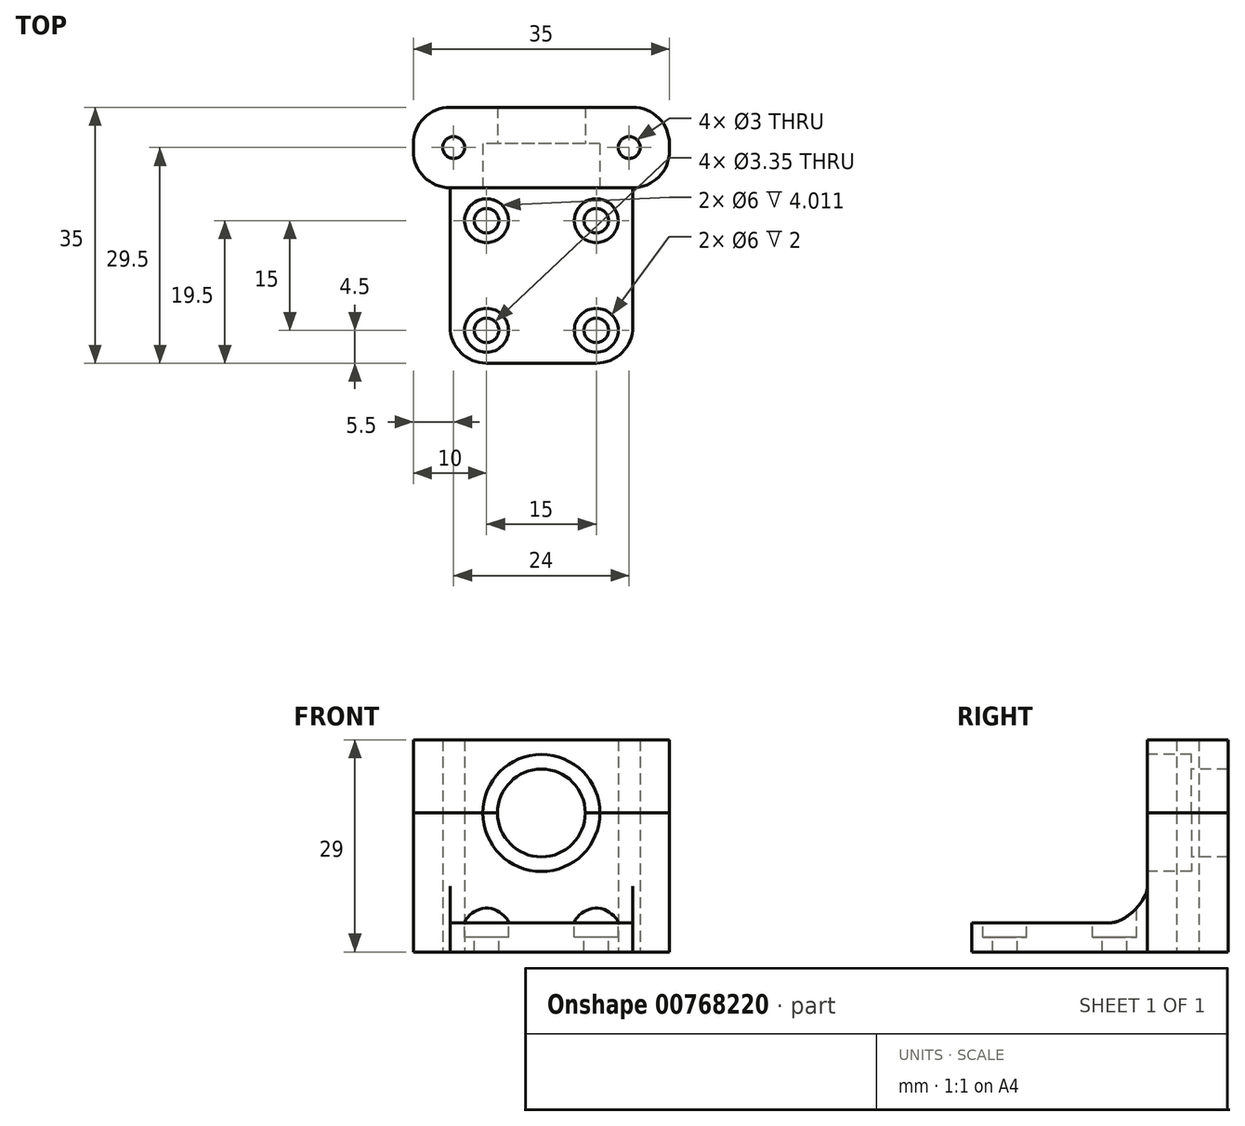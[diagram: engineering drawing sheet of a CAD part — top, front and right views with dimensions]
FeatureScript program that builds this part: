
annotation { "Feature Type Name" : "Feature", "Feature Type Description" : "" }
export const myFeature = defineFeature(function(context is Context, id is Id, definition is map)
    precondition{}
    {
        {
            var Q0;
            Q0=qCreatedBy(makeId("Right.planeOp"),FACE);
            var sketch = newSketch(context, id + "F0", { "sketchPlane" : qUnion([Q0])});
            skLineSegment(sketch, "E0", {"start": v(-12, -2) * mm, "end": v(23, -2) * mm});
            skLineSegment(sketch, "E1", {"start": v(23, -2) * mm, "end": v(23, 17) * mm});
            skLineSegment(sketch, "E2", {"start": v(23, 17) * mm, "end": v(12, 17) * mm});
            skLineSegment(sketch, "E3", {"start": v(12, 17) * mm, "end": v(12, 2) * mm});
            skLineSegment(sketch, "E4", {"start": v(12, 2) * mm, "end": v(-12, 2) * mm});
            skLineSegment(sketch, "E5", {"start": v(-12, 2) * mm, "end": v(-12, -2) * mm});
            skSolve(sketch);
        }
        {
            var Q0;
            Q0 = qSketchRegion(id + "F0", true);
            extrude(context, id + "F1", {"entities" : qUnion([Q0]), "endBound" : BoundingType.SYMMETRIC, "depth" : 25 * mm, "offsetDistance" : 25 * mm});
        }
        {
            var Q0;
            Q0=makeQuery(id+"F1.opExtrude","SWEPT_FACE",FACE,{"disambiguationData":[OSD([sQuery(id+"F0.wireOp",EDGE,"E0")])]});
            var sketch = newSketch(context, id + "F2", { "sketchPlane" : qUnion([Q0])});
            skLineSegment(sketch, "E6.bottom", {"start": v(-17.5, -23) * mm, "end": v(17.5, -23) * mm});
            skLineSegment(sketch, "E6.top", {"start": v(-17.5, -12) * mm, "end": v(17.5, -12) * mm});
            skLineSegment(sketch, "E6.left", {"start": v(-17.5, -23) * mm, "end": v(-17.5, -12) * mm});
            skLineSegment(sketch, "E6.right", {"start": v(17.5, -23) * mm, "end": v(17.5, -12) * mm});
            skSolve(sketch);
        }
        {
            var Q0;
            Q0 = qSketchRegion(id + "F2", true);
            var Q1;
            Q1=makeQuery(id+"F1.opExtrude","SWEPT_FACE",FACE,{"disambiguationData":[OSD([sQuery(id+"F0.wireOp",EDGE,"E2")])]});
            extrude(context, id + "F3", {"entities" : qUnion([Q0]), "operationType" : NewBodyOperationType.ADD, "endBound" : BoundingType.UP_TO_SURFACE, "oppositeDirection" : true, "depth" : 25 * mm, "endBoundEntityFace" : qUnion([Q1]), "offsetDistance" : 25 * mm});
        }
        {
            var Q0;
            Q0=makeQuery(id+"F1.opExtrude","SWEPT_FACE",FACE,{"disambiguationData":[OSD([sQuery(id+"F0.wireOp",EDGE,"E4")])]});
            var sketch = newSketch(context, id + "F4", { "sketchPlane" : qUnion([Q0])});
            skLineSegment(sketch, "E7.bottom", {"start": v(7.5, -7.5) * mm, "end": v(-7.5, -7.5) * mm, "construction": true});
            skLineSegment(sketch, "E7.top", {"start": v(7.5, 7.5) * mm, "end": v(-7.5, 7.5) * mm, "construction": true});
            skLineSegment(sketch, "E7.left", {"start": v(7.5, -7.5) * mm, "end": v(7.5, 7.5) * mm, "construction": true});
            skLineSegment(sketch, "E7.right", {"start": v(-7.5, -7.5) * mm, "end": v(-7.5, 7.5) * mm, "construction": true});
            skPoint(sketch, "E7.middle", {"position": v(0, 0) * mm});
            skCircle(sketch, "E8", {"center": v(7.5, 7.5) * mm, "radius": 3 * mm});
            skCircle(sketch, "E9", {"center": v(7.5, 7.5) * mm, "radius": 1.68 * mm});
            skCircle(sketch, "E10", {"center": v(7.5, -7.5) * mm, "radius": 3 * mm});
            skCircle(sketch, "E11", {"center": v(7.5, -7.5) * mm, "radius": 1.68 * mm});
            skCircle(sketch, "E12", {"center": v(-7.5, -7.5) * mm, "radius": 3 * mm});
            skCircle(sketch, "E13", {"center": v(-7.5, -7.5) * mm, "radius": 1.68 * mm});
            skCircle(sketch, "E14", {"center": v(-7.5, 7.5) * mm, "radius": 3 * mm});
            skCircle(sketch, "E15", {"center": v(-7.5, 7.5) * mm, "radius": 1.68 * mm});
            skSolve(sketch);
        }
        {
            var Q0;
            Q0=makeQuery(id+"F4.imprint","IMPRINT",FACE,{"disambiguationData":[TD([[makeQuery(id+"F4.imprint","IMPRINT",EDGE,{"derivedFrom":sQuery(id+"F4.wireOp",EDGE,"E9")}),1.0]])]});
            var Q1;
            Q1=makeQuery(id+"F4.imprint","IMPRINT",FACE,{"disambiguationData":[TD([[makeQuery(id+"F4.imprint","IMPRINT",EDGE,{"derivedFrom":sQuery(id+"F4.wireOp",EDGE,"E11")}),1.0]])]});
            var Q2;
            Q2=makeQuery(id+"F4.imprint","IMPRINT",FACE,{"disambiguationData":[TD([[makeQuery(id+"F4.imprint","IMPRINT",EDGE,{"derivedFrom":sQuery(id+"F4.wireOp",EDGE,"E13")}),1.0]])]});
            var Q3;
            Q3=makeQuery(id+"F4.imprint","IMPRINT",FACE,{"disambiguationData":[TD([[makeQuery(id+"F4.imprint","IMPRINT",EDGE,{"derivedFrom":sQuery(id+"F4.wireOp",EDGE,"E15")}),1.0]])]});
            extrude(context, id + "F5", {"entities" : qUnion([Q0, Q1, Q2, Q3]), "operationType" : NewBodyOperationType.REMOVE, "endBound" : BoundingType.THROUGH_ALL, "oppositeDirection" : true, "depth" : 25 * mm, "offsetDistance" : 25 * mm});
        }
        {
            var Q0;
            Q0=makeQuery(id+"F4.imprint","IMPRINT",FACE,{"disambiguationData":[TD([[makeQuery(id+"F4.imprint","IMPRINT",EDGE,{"derivedFrom":sQuery(id+"F4.wireOp",EDGE,"E14")}),1.0]])]});
            var Q1;
            Q1=makeQuery(id+"F4.imprint","IMPRINT",FACE,{"disambiguationData":[TD([[makeQuery(id+"F4.imprint","IMPRINT",EDGE,{"derivedFrom":sQuery(id+"F4.wireOp",EDGE,"E8")}),1.0]])]});
            var Q2;
            Q2=makeQuery(id+"F4.imprint","IMPRINT",FACE,{"disambiguationData":[TD([[makeQuery(id+"F4.imprint","IMPRINT",EDGE,{"derivedFrom":sQuery(id+"F4.wireOp",EDGE,"E10")}),1.0]])]});
            var Q3;
            Q3=makeQuery(id+"F4.imprint","IMPRINT",FACE,{"disambiguationData":[TD([[makeQuery(id+"F4.imprint","IMPRINT",EDGE,{"derivedFrom":sQuery(id+"F4.wireOp",EDGE,"E12")}),1.0]])]});
            extrude(context, id + "F6", {"entities" : qUnion([Q0, Q1, Q2, Q3]), "operationType" : NewBodyOperationType.REMOVE, "oppositeDirection" : true, "depth" : 2 * mm, "offsetDistance" : 25 * mm});
        }
        {
            var Q0;
            {var subQ0=sQuery(id+"F0.wireOp",EDGE,"E2");Q0=makeQuery(id+"F3.boolean.opBoolean","MERGE",FACE,{"derivedFrom":[makeQuery(id+"F1.opExtrude","SWEPT_FACE",FACE,{"disambiguationData":[OSD([subQ0])]}),makeQuery(id+"F3.opExtrude","CAP_FACE",FACE,{"disambiguationData":[OSD([subQ0])],"isStart":false})]});}
            extrude(context, id + "F7", {"entities" : qUnion([Q0]), "depth" : 10 * mm, "offsetDistance" : 25 * mm});
        }
        {
            var Q0;
            Q0=makeQuery(id+"F3.boolean.opBoolean","MERGE",FACE,{"derivedFrom":[makeQuery(id+"F1.opExtrude","SWEPT_FACE",FACE,{"disambiguationData":[OSD([sQuery(id+"F0.wireOp",EDGE,"E0")])]}),makeQuery(id+"F3.opExtrude","CAP_FACE",FACE,{"disambiguationData":[OSD([sQuery(id+"F2.wireOp",EDGE,"E6.bottom"),sQuery(id+"F2.wireOp",EDGE,"E6.top"),sQuery(id+"F2.wireOp",EDGE,"E6.left"),sQuery(id+"F2.wireOp",EDGE,"E6.right")])],"isStart":true})]});
            var sketch = newSketch(context, id + "F8", { "sketchPlane" : qUnion([Q0])});
            skLineSegment(sketch, "E16", {"start": v(-17.5, -17.5) * mm, "end": v(17.5, -17.5) * mm, "construction": true});
            skCircle(sketch, "E17", {"center": v(-12, -17.5) * mm, "radius": 1.5 * mm});
            skCircle(sketch, "E18", {"center": v(12, -17.5) * mm, "radius": 1.5 * mm});
            skSolve(sketch);
        }
        {
            var Q0;
            Q0 = qSketchRegion(id + "F8", true);
            extrude(context, id + "F9", {"entities" : qUnion([Q0]), "operationType" : NewBodyOperationType.REMOVE, "endBound" : BoundingType.THROUGH_ALL, "oppositeDirection" : true, "depth" : 25 * mm, "offsetDistance" : 25 * mm});
        }
        {
            var Q0;
            Q0=makeQuery(id+"F3.boolean.opBoolean","MERGE",FACE,{"derivedFrom":[makeQuery(id+"F1.opExtrude","SWEPT_FACE",FACE,{"disambiguationData":[OSD([sQuery(id+"F0.wireOp",EDGE,"E3")])]}),makeQuery(id+"F3.opExtrude","SWEPT_FACE",FACE,{"disambiguationData":[OSD([sQuery(id+"F2.wireOp",EDGE,"E6.top")])]})]});
            var sketch = newSketch(context, id + "F10", { "sketchPlane" : qUnion([Q0])});
            skCircle(sketch, "E19", {"center": v(0, 17) * mm, "radius": 8 * mm});
            skCircle(sketch, "E20", {"center": v(0, 17) * mm, "radius": 6 * mm});
            skSolve(sketch);
        }
        {
            var Q0;
            {var subQ0=sQuery(id+"F10.wireOp",EDGE,"E20");var subQ1=sQuery(id+"F2.wireOp",EDGE,"E6.top");var subQ2=sQuery(id+"F0.wireOp",EDGE,"E0");var subQ4=makeQuery(id+"F2.imprint","INTERSECT",VERTEX,{"derivedFrom":[makeQuery(id+"F1.opExtrude","CAP_EDGE",EDGE,{"disambiguationData":[OSD([subQ2])],"isStart":true}),subQ1]});var subQ5=sQuery(id+"F0.wireOp",EDGE,"E2");var subQ6=makeQuery(id+"F3.boolean.opBoolean","MERGE",EDGE,{"derivedFrom":[makeQuery(id+"F1.opExtrude","SWEPT_EDGE",EDGE,{"disambiguationData":[OSD([subQ5,sQuery(id+"F0.wireOp",EDGE,"E3")])]}),makeQuery(id+"F3.opExtrude","TWEAK_EDGE",EDGE,{"derivedFrom":[makeQuery(id+"F1.opExtrude","SWEPT_FACE",FACE,{"disambiguationData":[OSD([subQ5])]}),makeQuery(id+"F2.imprint","IMPRINT",EDGE,{"disambiguationData":[TD([[makeQuery(id+"F2.imprint","INTERSECT",VERTEX,{"derivedFrom":[subQ1,sQuery(id+"F2.wireOp",EDGE,"E6.left")]}),-1.0]])],"derivedFrom":subQ1}),makeQuery(id+"F2.imprint","IMPRINT",EDGE,{"disambiguationData":[TD([[subQ4,-1.0]])],"derivedFrom":subQ1}),makeQuery(id+"F2.imprint","IMPRINT",EDGE,{"disambiguationData":[TD([[makeQuery(id+"F2.imprint","INTERSECT",VERTEX,{"derivedFrom":[subQ1,sQuery(id+"F2.wireOp",EDGE,"E6.right")]}),1.0]])],"derivedFrom":subQ1})]})]});var subQ7=makeQuery(id+"F10.imprint","INTERSECT",VERTEX,{"disambiguationData":[OD(0.0)],"derivedFrom":[subQ6,subQ0]});Q0=makeQuery(id+"F10.imprint","IMPRINT",FACE,{"disambiguationData":[TD([[makeQuery(id+"F10.imprint","IMPRINT",EDGE,{"disambiguationData":[TD([[subQ7,-1.0]])],"derivedFrom":subQ0}),1.0]])]});}
            var Q1;
            {var subQ0=sQuery(id+"F10.wireOp",EDGE,"E20");var subQ1=sQuery(id+"F2.wireOp",EDGE,"E6.top");var subQ2=sQuery(id+"F0.wireOp",EDGE,"E0");var subQ4=makeQuery(id+"F2.imprint","INTERSECT",VERTEX,{"derivedFrom":[makeQuery(id+"F1.opExtrude","CAP_EDGE",EDGE,{"disambiguationData":[OSD([subQ2])],"isStart":true}),subQ1]});var subQ5=sQuery(id+"F0.wireOp",EDGE,"E2");var subQ6=makeQuery(id+"F3.boolean.opBoolean","MERGE",EDGE,{"derivedFrom":[makeQuery(id+"F1.opExtrude","SWEPT_EDGE",EDGE,{"disambiguationData":[OSD([subQ5,sQuery(id+"F0.wireOp",EDGE,"E3")])]}),makeQuery(id+"F3.opExtrude","TWEAK_EDGE",EDGE,{"derivedFrom":[makeQuery(id+"F1.opExtrude","SWEPT_FACE",FACE,{"disambiguationData":[OSD([subQ5])]}),makeQuery(id+"F2.imprint","IMPRINT",EDGE,{"disambiguationData":[TD([[makeQuery(id+"F2.imprint","INTERSECT",VERTEX,{"derivedFrom":[subQ1,sQuery(id+"F2.wireOp",EDGE,"E6.left")]}),-1.0]])],"derivedFrom":subQ1}),makeQuery(id+"F2.imprint","IMPRINT",EDGE,{"disambiguationData":[TD([[subQ4,-1.0]])],"derivedFrom":subQ1}),makeQuery(id+"F2.imprint","IMPRINT",EDGE,{"disambiguationData":[TD([[makeQuery(id+"F2.imprint","INTERSECT",VERTEX,{"derivedFrom":[subQ1,sQuery(id+"F2.wireOp",EDGE,"E6.right")]}),1.0]])],"derivedFrom":subQ1})]})]});var subQ7=makeQuery(id+"F10.imprint","INTERSECT",VERTEX,{"disambiguationData":[OD(0.0)],"derivedFrom":[subQ6,subQ0]});Q1=makeQuery(id+"F10.imprint","IMPRINT",FACE,{"disambiguationData":[TD([[makeQuery(id+"F10.imprint","IMPRINT",EDGE,{"disambiguationData":[TD([[subQ7,1.0]])],"derivedFrom":subQ0}),1.0]])]});}
            var Q2;
            Q2=sQuery(id+"F10.wireOp",EDGE,"E20");
            extrude(context, id + "F11", {"entities" : qUnion([Q0, Q1]), "operationType" : NewBodyOperationType.REMOVE, "surfaceEntities" : qUnion([Q2]), "endBound" : BoundingType.THROUGH_ALL, "oppositeDirection" : true, "depth" : 25 * mm, "offsetDistance" : 25 * mm});
        }
        {
            var Q0;
            {var subQ0=sQuery(id+"F10.wireOp",EDGE,"E19");var subQ1=sQuery(id+"F2.wireOp",EDGE,"E6.top");var subQ2=sQuery(id+"F0.wireOp",EDGE,"E0");var subQ4=makeQuery(id+"F2.imprint","INTERSECT",VERTEX,{"derivedFrom":[makeQuery(id+"F1.opExtrude","CAP_EDGE",EDGE,{"disambiguationData":[OSD([subQ2])],"isStart":true}),subQ1]});var subQ5=sQuery(id+"F0.wireOp",EDGE,"E2");var subQ6=makeQuery(id+"F3.boolean.opBoolean","MERGE",EDGE,{"derivedFrom":[makeQuery(id+"F1.opExtrude","SWEPT_EDGE",EDGE,{"disambiguationData":[OSD([subQ5,sQuery(id+"F0.wireOp",EDGE,"E3")])]}),makeQuery(id+"F3.opExtrude","TWEAK_EDGE",EDGE,{"derivedFrom":[makeQuery(id+"F1.opExtrude","SWEPT_FACE",FACE,{"disambiguationData":[OSD([subQ5])]}),makeQuery(id+"F2.imprint","IMPRINT",EDGE,{"disambiguationData":[TD([[makeQuery(id+"F2.imprint","INTERSECT",VERTEX,{"derivedFrom":[subQ1,sQuery(id+"F2.wireOp",EDGE,"E6.left")]}),-1.0]])],"derivedFrom":subQ1}),makeQuery(id+"F2.imprint","IMPRINT",EDGE,{"disambiguationData":[TD([[subQ4,-1.0]])],"derivedFrom":subQ1}),makeQuery(id+"F2.imprint","IMPRINT",EDGE,{"disambiguationData":[TD([[makeQuery(id+"F2.imprint","INTERSECT",VERTEX,{"derivedFrom":[subQ1,sQuery(id+"F2.wireOp",EDGE,"E6.right")]}),1.0]])],"derivedFrom":subQ1})]})]});var subQ7=makeQuery(id+"F10.imprint","INTERSECT",VERTEX,{"disambiguationData":[OD(0.0)],"derivedFrom":[subQ6,subQ0]});Q0=makeQuery(id+"F10.imprint","IMPRINT",FACE,{"disambiguationData":[TD([[makeQuery(id+"F10.imprint","IMPRINT",EDGE,{"disambiguationData":[TD([[subQ7,1.0]])],"derivedFrom":subQ0}),1.0]])]});}
            var Q1;
            {var subQ0=sQuery(id+"F10.wireOp",EDGE,"E19");var subQ1=sQuery(id+"F2.wireOp",EDGE,"E6.top");var subQ2=sQuery(id+"F0.wireOp",EDGE,"E0");var subQ4=makeQuery(id+"F2.imprint","INTERSECT",VERTEX,{"derivedFrom":[makeQuery(id+"F1.opExtrude","CAP_EDGE",EDGE,{"disambiguationData":[OSD([subQ2])],"isStart":true}),subQ1]});var subQ5=sQuery(id+"F0.wireOp",EDGE,"E2");var subQ6=makeQuery(id+"F3.boolean.opBoolean","MERGE",EDGE,{"derivedFrom":[makeQuery(id+"F1.opExtrude","SWEPT_EDGE",EDGE,{"disambiguationData":[OSD([subQ5,sQuery(id+"F0.wireOp",EDGE,"E3")])]}),makeQuery(id+"F3.opExtrude","TWEAK_EDGE",EDGE,{"derivedFrom":[makeQuery(id+"F1.opExtrude","SWEPT_FACE",FACE,{"disambiguationData":[OSD([subQ5])]}),makeQuery(id+"F2.imprint","IMPRINT",EDGE,{"disambiguationData":[TD([[makeQuery(id+"F2.imprint","INTERSECT",VERTEX,{"derivedFrom":[subQ1,sQuery(id+"F2.wireOp",EDGE,"E6.left")]}),-1.0]])],"derivedFrom":subQ1}),makeQuery(id+"F2.imprint","IMPRINT",EDGE,{"disambiguationData":[TD([[subQ4,-1.0]])],"derivedFrom":subQ1}),makeQuery(id+"F2.imprint","IMPRINT",EDGE,{"disambiguationData":[TD([[makeQuery(id+"F2.imprint","INTERSECT",VERTEX,{"derivedFrom":[subQ1,sQuery(id+"F2.wireOp",EDGE,"E6.right")]}),1.0]])],"derivedFrom":subQ1})]})]});var subQ7=makeQuery(id+"F10.imprint","INTERSECT",VERTEX,{"disambiguationData":[OD(0.0)],"derivedFrom":[subQ6,subQ0]});Q1=makeQuery(id+"F10.imprint","IMPRINT",FACE,{"disambiguationData":[TD([[makeQuery(id+"F10.imprint","IMPRINT",EDGE,{"disambiguationData":[TD([[subQ7,-1.0]])],"derivedFrom":subQ0}),1.0]])]});}
            extrude(context, id + "F12", {"entities" : qUnion([Q0, Q1]), "operationType" : NewBodyOperationType.REMOVE, "oppositeDirection" : true, "depth" : 6 * mm, "offsetDistance" : 25 * mm});
        }
        {
            var Q0;
            Q0=makeQuery(id+"F3.opExtrude","SWEPT_EDGE",EDGE,{"disambiguationData":[OSD([sQuery(id+"F2.wireOp",EDGE,"E6.top"),sQuery(id+"F2.wireOp",EDGE,"E6.left")])]});
            var Q1;
            Q1=makeQuery(id+"F7.opExtrude","SWEPT_EDGE",EDGE,{"disambiguationData":[OSD([sQuery(id+"F0.wireOp",EDGE,"E2"),sQuery(id+"F2.wireOp",EDGE,"E6.top"),sQuery(id+"F2.wireOp",EDGE,"E6.left")])]});
            var Q2;
            Q2=makeQuery(id+"F7.opExtrude","SWEPT_EDGE",EDGE,{"disambiguationData":[OSD([sQuery(id+"F0.wireOp",EDGE,"E2"),sQuery(id+"F2.wireOp",EDGE,"E6.bottom"),sQuery(id+"F2.wireOp",EDGE,"E6.left")])]});
            var Q3;
            Q3=makeQuery(id+"F3.opExtrude","SWEPT_EDGE",EDGE,{"disambiguationData":[OSD([sQuery(id+"F2.wireOp",EDGE,"E6.bottom"),sQuery(id+"F2.wireOp",EDGE,"E6.left")])]});
            var Q4;
            Q4=makeQuery(id+"F3.opExtrude","SWEPT_EDGE",EDGE,{"disambiguationData":[OSD([sQuery(id+"F2.wireOp",EDGE,"E6.top"),sQuery(id+"F2.wireOp",EDGE,"E6.right")])]});
            var Q5;
            Q5=makeQuery(id+"F7.opExtrude","SWEPT_EDGE",EDGE,{"disambiguationData":[OSD([sQuery(id+"F0.wireOp",EDGE,"E2"),sQuery(id+"F2.wireOp",EDGE,"E6.top"),sQuery(id+"F2.wireOp",EDGE,"E6.right")])]});
            var Q6;
            Q6=makeQuery(id+"F7.opExtrude","SWEPT_EDGE",EDGE,{"disambiguationData":[OSD([sQuery(id+"F0.wireOp",EDGE,"E2"),sQuery(id+"F2.wireOp",EDGE,"E6.bottom"),sQuery(id+"F2.wireOp",EDGE,"E6.right")])]});
            var Q7;
            Q7=makeQuery(id+"F3.opExtrude","SWEPT_EDGE",EDGE,{"disambiguationData":[OSD([sQuery(id+"F2.wireOp",EDGE,"E6.bottom"),sQuery(id+"F2.wireOp",EDGE,"E6.right")])]});
            var Q8;
            Q8=makeQuery(id+"F1.opExtrude","CAP_EDGE",EDGE,{"disambiguationData":[OSD([sQuery(id+"F0.wireOp",EDGE,"E5")])],"isStart":false});
            var Q9;
            Q9=makeQuery(id+"F1.opExtrude","CAP_EDGE",EDGE,{"disambiguationData":[OSD([sQuery(id+"F0.wireOp",EDGE,"E5")])],"isStart":true});
            fillet(context, id + "F13", {"entities" : qUnion([Q0, Q1, Q2, Q3, Q4, Q5, Q6, Q7, Q8, Q9]), "radius" : 5 * mm, "tangentPropagation" : true, "allowEdgeOverflow" : false});
        }
        {
            var Q0;
            Q0=makeQuery(id+"F1.opExtrude","SWEPT_EDGE",EDGE,{"disambiguationData":[OSD([sQuery(id+"F0.wireOp",EDGE,"E3"),sQuery(id+"F0.wireOp",EDGE,"E4")])]});
            fillet(context, id + "F14", {"entities" : qUnion([Q0]), "radius" : 5 * mm, "tangentPropagation" : true, "rho" : .3, "crossSection" : FilletCrossSection.CONIC, "allowEdgeOverflow" : false});
        }
    });
